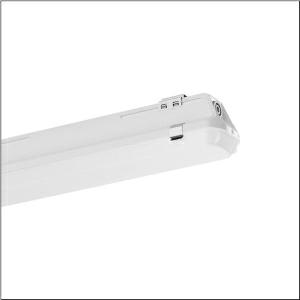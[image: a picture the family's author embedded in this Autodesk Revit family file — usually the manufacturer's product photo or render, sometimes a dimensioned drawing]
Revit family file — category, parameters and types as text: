
# Revit family: monsun_r__11_parking_51fg207p440h_0f51
name_source: partatom
category: Lighting Fixtures
units: mm (PartAtom-declared; Revit-internal decimal feet)

## family parameters
Cut with Voids When Loaded = No
Host = Face
Light Source = No
Part Type = Normal
Room Calculation Point = No
Round Connector Dimension = Use Diameter
Shared = No

## types (1)
- Monsun® 11 parking (1 x LED, 4820 lm, 29.2 W, 4000K)
    Apparent Load = 29 VA
    CIE Flux Codes = 45 75 93 94 100
    Color Rendering = 80
    Color Temperature = 4000K
    Default Elevation = 1800 mm
    Description = Monsun® 11 parking, damp-proof luminaire, chain hanger, primary optical cover: enclosure, of PC, light emission: direct distribution, primary light characteristic: symmetric, installation type: suspended mounting, surface-mounted, horizontal mounting, vertical mounting, LED, rated luminous flux: 4.820lm, luminous efficacy: 165lm/W, light colour: 840, colour temperature: 4000K, control gear: ECG, with terminal, 3-pole, max. 2.5mm², mains connection: 220..240V, AC, 50/60Hz, rated input power: 29W, housing, of glass-fibre reinforced polyester, uncoated, bright grey, incl. chain hanger, length: 1.590mm, width: 90mm, height: 88mm, clip for enclosure, of stainless steel (V2A), ceiling mounting element, of stainless steel (V2A), chain hanger, of stainless steel (V2A), protection rating (complete): IP66, insulation class (complete): insulation class I (protective earthing), certification: CE, ENEC, VDE, UKCA, protection symbol: D, impact resistance: IK08, permissible operating ambient temperature: -35..+40°C, standard: EN 50419, EN 60598-2-1, no direct snow, no direct sun, no direct rain, for indoor or canopied outdoor use, corresponds to IFS (International Featured Standards) requirements for safety and quality in the food industry, contact your sales advisor before using the luminaires in applications with unclear chemical exposure, large temperature fluctuations or condensation-forming humidity, LABS conformity tested according to VDMA 24364:2018-05, packaging unit: 1 piece
    Height = 89 mm
    Lamp = 1 x LED
    Lamp Light Flux = 4820 lm
    Lamp Power = 29.2 W
    Lamp count = 1
    Length = 1590 mm
    Luminous efficacy = 165 lm/W
    Manufacturer = Siteco
    ModVariant = No
    Model = 51FG207P440H
    Mounting Place = Ceiling
    Mounting Type = Surface mounted
    Number of Poles = 1
    OnlyDefault = Yes
    Power Factor = 1
    Product Name = Monsun® 11 parking
    Product group = damp-proof luminaire
    ProductGroupID = 300
    Protection Class = Protection class I
    Protection Degree = IP 66
    RLX_Detail_Level = 1
    RLX_Emergency_Light_Flux = 0 lm
    RLX_Emergency_Type = 0
    RLX_Emergency_Type_DB = No
    RlxData = <blob elided: 88945 chars, md5=18573334>
    Socket = socket
    Standby Power = 0 W
    System Light Flux = 4820 lm
    System Power = 29 W
    Type Comments = Product without accessories
    Type Image = l_1319650.jpg
    URL = http://relux.com
    VarID = ---
    Voltage = 0 V
    Weight = 0.00 kg
    Width = 90 mm

## geometry (parser evidence)
native form markers: Blend x4, Sweep x13
no freeform markers — native parametric forms only
